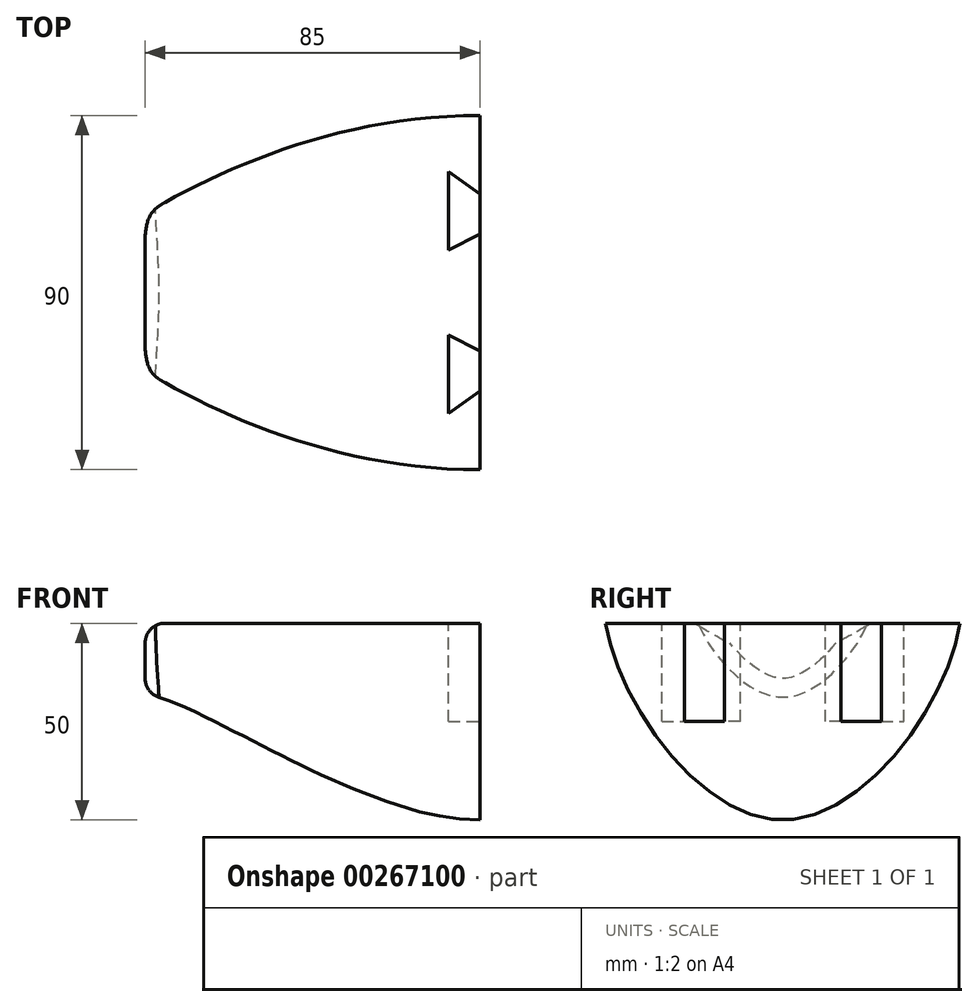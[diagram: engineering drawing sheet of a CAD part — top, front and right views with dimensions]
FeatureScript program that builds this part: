
annotation { "Feature Type Name" : "Feature", "Feature Type Description" : "" }
export const myFeature = defineFeature(function(context is Context, id is Id, definition is map)
    precondition{}
    {
        {
            var Q0;
            Q0=qCreatedBy(makeId("Right.planeOp"),FACE);
            cPlane(context, id + "F0", {"entities" : qUnion([Q0]), "cplaneType" : CPlaneType.OFFSET, "offset" : 85 * mm, "oppositeDirection" : true, "width" : 150 * mm, "height" : 150 * mm});
        }
        {
            var Q0;
            Q0=qCreatedBy(makeId("Right.planeOp"),FACE);
            var sketch = newSketch(context, id + "F1", { "sketchPlane" : qUnion([Q0])});
            skFitSpline(sketch, "E0", {"points": [v(-45, 0) * mm, v(0, -50) * mm, v(45, 0) * mm], "startDerivative": vector(18, -120) * mm, "endDerivative": vector(18, 120) * mm});
            skLineSegment(sketch, "E1", {"start": v(-45, 0) * mm, "end": v(0, 0) * mm});
            skLineSegment(sketch, "E2", {"start": v(0, 0) * mm, "end": v(45, 0) * mm});
            skSolve(sketch);
        }
        {
            var Q0;
            Q0=qCreatedBy(id+"F0.planeOp",FACE);
            var sketch = newSketch(context, id + "F2", { "sketchPlane" : qUnion([Q0])});
            skFitSpline(sketch, "E3", {"points": [v(-20, 0) * mm, v(0, -18) * mm, v(20, 0) * mm], "startDerivative": vector(12, -30) * mm, "endDerivative": vector(12, 30) * mm});
            skLineSegment(sketch, "E4", {"start": v(-20, 0) * mm, "end": v(0, 0) * mm});
            skLineSegment(sketch, "E5", {"start": v(0, 0) * mm, "end": v(20, 0) * mm});
            skSolve(sketch);
        }
        {
            var Q0;
            Q0=qCreatedBy(makeId("Top.planeOp"),FACE);
            var sketch = newSketch(context, id + "F3", { "sketchPlane" : qUnion([Q0])});
            skPoint(sketch, "E6.0", {"position": v(0, 45) * mm});
            skPoint(sketch, "E7.0", {"position": v(-85, 20) * mm});
            skFitSpline(sketch, "E8", {"points": [v(0, 45) * mm, v(-85, 20) * mm], "startDerivative": vector(-105, 0) * mm, "endDerivative": vector(-60, -36) * mm});
            skPoint(sketch, "E9.0", {"position": v(0, -45) * mm});
            skPoint(sketch, "E10.0", {"position": v(-85, -20) * mm});
            skFitSpline(sketch, "E11", {"points": [v(0, -45) * mm, v(-85, -20) * mm], "startDerivative": vector(-105, 0) * mm, "endDerivative": vector(-60, 36) * mm});
            skSolve(sketch);
        }
        {
            var Q0;
            Q0=qCreatedBy(makeId("Front.planeOp"),FACE);
            var sketch = newSketch(context, id + "F4", { "sketchPlane" : qUnion([Q0])});
            skPoint(sketch, "E12.0", {"position": v(0, -50) * mm});
            skPoint(sketch, "E13.0", {"position": v(-85, -18) * mm});
            skFitSpline(sketch, "E14", {"points": [v(0, -50) * mm, v(-85, -18) * mm], "startDerivative": vector(-89.92, 0) * mm, "endDerivative": vector(-45, 6) * mm});
            skSolve(sketch);
        }
        {
            var Q0;
            Q0=makeQuery(id+"F1.imprint","IMPRINT",FACE,{"disambiguationData":[TD([[makeQuery(id+"F1.imprint","IMPRINT",EDGE,{"derivedFrom":sQuery(id+"F1.wireOp",EDGE,"E0")}),1.0]])]});
            var Q1;
            Q1=makeQuery(id+"F2.imprint","IMPRINT",FACE,{"disambiguationData":[TD([[makeQuery(id+"F2.imprint","IMPRINT",EDGE,{"derivedFrom":sQuery(id+"F2.wireOp",EDGE,"E3")}),1.0]])]});
            var Q2;
            Q2=sQuery(id+"F3.wireOp",EDGE,"E11");
            var Q3;
            Q3=sQuery(id+"F4.wireOp",EDGE,"E14");
            var Q4;
            Q4=sQuery(id+"F3.wireOp",EDGE,"E8");
            loft(context, id + "F5", {"addGuides" : true, "sheetProfilesArray" : [{ "sheetProfileEntities" : qUnion([Q0]) }, { "sheetProfileEntities" : qUnion([Q1]) }], "guidesArray" : [{ "guideEntities" : qUnion([Q2]), "guideDerivativeType" : LoftGuideDerivativeType.DEFAULT, "guideDerivativeMagnitude" : 1 }, { "guideEntities" : qUnion([Q3]), "guideDerivativeType" : LoftGuideDerivativeType.DEFAULT, "guideDerivativeMagnitude" : 1 }, { "guideEntities" : qUnion([Q4]), "guideDerivativeType" : LoftGuideDerivativeType.DEFAULT, "guideDerivativeMagnitude" : 1 }]});
        }
        {
            var Q0;
            Q0=makeQuery(id+"F5.opLoft","MID_CAP_EDGE",EDGE,{"disambiguationData":[OSD([sQuery(id+"F2.wireOp",EDGE,"E3"),sQuery(id+"F3.wireOp",EDGE,"E8"),sQuery(id+"F4.wireOp",EDGE,"E14")])],"capPos":1.0});
            fillet(context, id + "F6", {"entities" : qUnion([Q0]), "radius" : 5 * mm, "tangentPropagation" : true, "allowEdgeOverflow" : false});
        }
        {
            var Q0;
            Q0=makeQuery(id+"F5.opLoft","SWEPT_FACE",FACE,{"disambiguationData":[OSD([sQuery(id+"F1.wireOp",EDGE,"E1"),sQuery(id+"F1.wireOp",EDGE,"E2"),sQuery(id+"F2.wireOp",EDGE,"E4"),sQuery(id+"F2.wireOp",EDGE,"E5"),sQuery(id+"F3.wireOp",EDGE,"E8")])]});
            var sketch = newSketch(context, id + "F7", { "sketchPlane" : qUnion([Q0])});
            skLineSegment(sketch, "E15", {"start": v(0, 25) * mm, "end": v(-8, 30.76) * mm});
            skLineSegment(sketch, "E16", {"start": v(-8, 30.76) * mm, "end": v(-8, 10.76) * mm});
            skLineSegment(sketch, "E17", {"start": v(-8, 10.76) * mm, "end": v(0.36, 15) * mm});
            skLineSegment(sketch, "E18", {"start": v(0.36, 15) * mm, "end": v(0, 25) * mm});
            skLineSegment(sketch, "E19.MirrorCS", {"start": v(-8, -30.76) * mm, "end": v(-8, -10.76) * mm});
            skLineSegment(sketch, "E20.MirrorCS", {"start": v(-8, -10.76) * mm, "end": v(0.36, -15) * mm});
            skLineSegment(sketch, "E21.MirrorCS", {"start": v(0.36, -15) * mm, "end": v(0, -25) * mm});
            skLineSegment(sketch, "E22.MirrorCS", {"start": v(0, -25) * mm, "end": v(-8, -30.76) * mm});
            skSolve(sketch);
        }
        {
            var Q0;
            {var subQ0=sQuery(id+"F7.wireOp",EDGE,"E15");Q0=makeQuery(id+"F7.imprint","IMPRINT",FACE,{"disambiguationData":[TD([[makeQuery(id+"F7.imprint","IMPRINT",EDGE,{"derivedFrom":subQ0}),1.0]])]});}
            var Q1;
            Q1=makeQuery(id+"F7.imprint","IMPRINT",FACE,{"disambiguationData":[TD([[makeQuery(id+"F7.imprint","IMPRINT",EDGE,{"derivedFrom":sQuery(id+"F7.wireOp",EDGE,"E19.MirrorCS")}),-1.0]])]});
            extrude(context, id + "F8", {"entities" : qUnion([Q0, Q1]), "operationType" : NewBodyOperationType.REMOVE, "oppositeDirection" : true, "depth" : 25 * mm});
        }
    });
